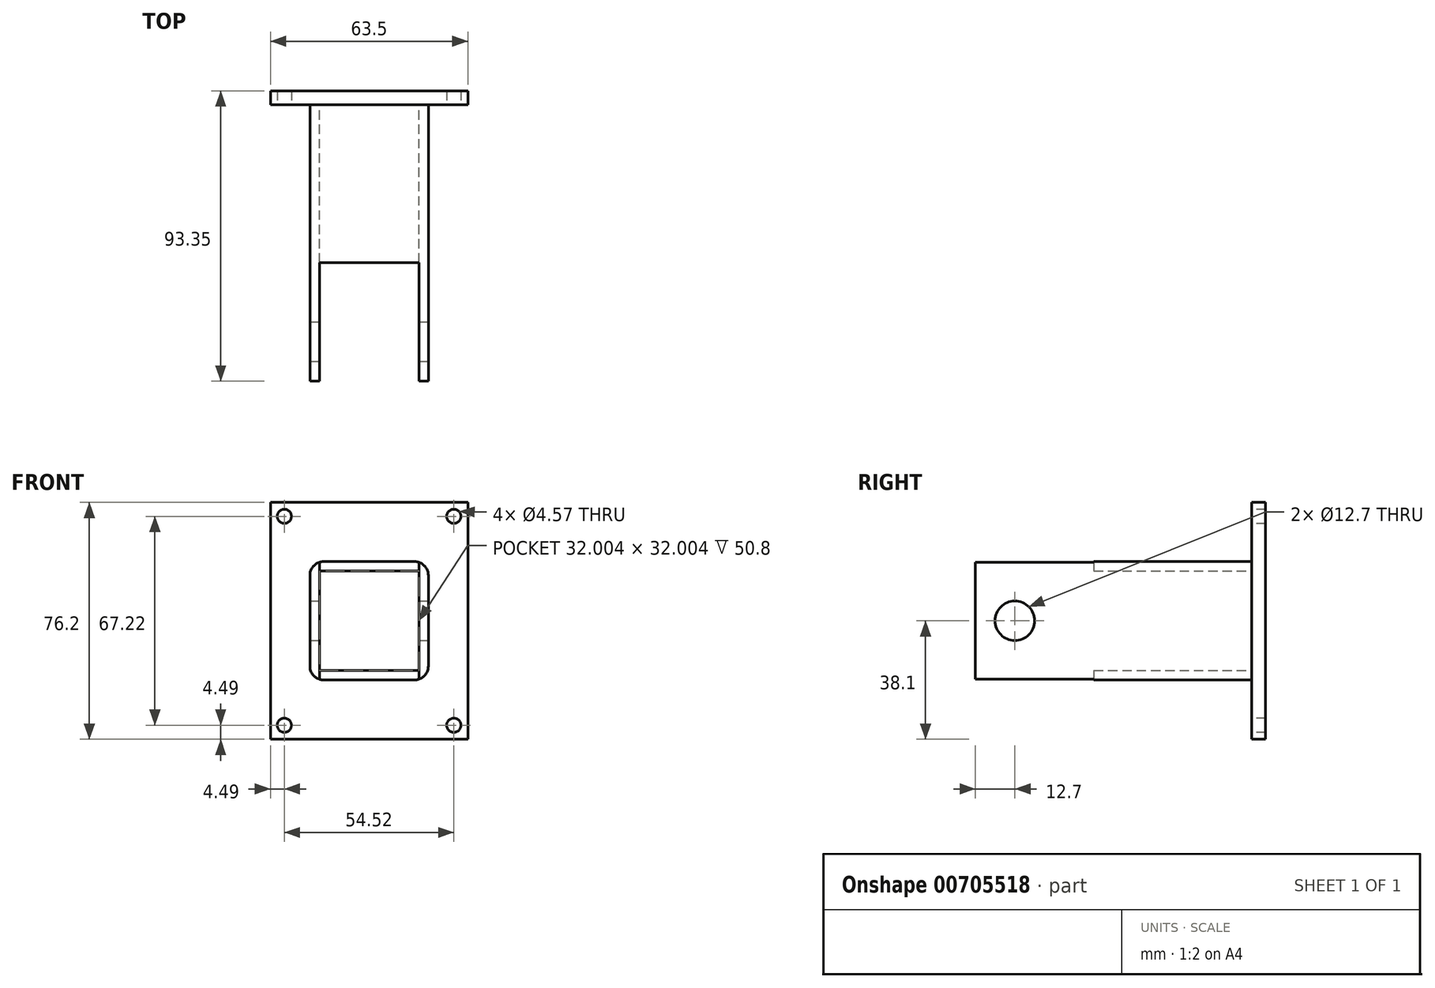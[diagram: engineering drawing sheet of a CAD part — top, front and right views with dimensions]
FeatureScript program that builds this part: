
annotation { "Feature Type Name" : "Feature", "Feature Type Description" : "" }
export const myFeature = defineFeature(function(context is Context, id is Id, definition is map)
    precondition{}
    {
        {
            var Q0;
            Q0=qCreatedBy(makeId("Front.planeOp"),FACE);
            var sketch = newSketch(context, id + "F0", { "sketchPlane" : qUnion([Q0])});
            skLineSegment(sketch, "E0.bottom", {"start": v(14.6, 19.05) * mm, "end": v(-14.6, 19.05) * mm});
            skLineSegment(sketch, "E0.top", {"start": v(14.6, -19.05) * mm, "end": v(-14.6, -19.05) * mm});
            skLineSegment(sketch, "E0.left", {"start": v(19.05, 14.6) * mm, "end": v(19.05, -14.6) * mm});
            skLineSegment(sketch, "E0.right", {"start": v(-19.05, 14.6) * mm, "end": v(-19.05, -14.6) * mm});
            skPoint(sketch, "E0.middle", {"position": v(0, 0) * mm});
            skPoint(sketch, "E1.visualSharp", {"position": v(-19.05, 19.05) * mm});
            skArc(sketch, "E1.filletArc", {"start": v(-14.6, 19.05) * mm, "mid": v(-17.75, 17.75) * mm, "end": v(-19.05, 14.6) * mm});
            skPoint(sketch, "E2.visualSharp", {"position": v(19.05, 19.05) * mm});
            skArc(sketch, "E2.filletArc", {"start": v(19.05, 14.6) * mm, "mid": v(17.75, 17.75) * mm, "end": v(14.6, 19.05) * mm});
            skPoint(sketch, "E3.visualSharp", {"position": v(19.05, -19.05) * mm});
            skArc(sketch, "E3.filletArc", {"start": v(14.6, -19.05) * mm, "mid": v(17.75, -17.75) * mm, "end": v(19.05, -14.6) * mm});
            skPoint(sketch, "E4.visualSharp", {"position": v(-19.05, -19.05) * mm});
            skArc(sketch, "E4.filletArc", {"start": v(-19.05, -14.6) * mm, "mid": v(-17.75, -17.75) * mm, "end": v(-14.6, -19.05) * mm});
            skLineSegment(sketch, "E5.0", {"start": v(16, 16) * mm, "end": v(-16, 16) * mm});
            skLineSegment(sketch, "E5.1", {"start": v(16, 16) * mm, "end": v(16, -16) * mm});
            skLineSegment(sketch, "E5.2", {"start": v(16, -16) * mm, "end": v(-16, -16) * mm});
            skLineSegment(sketch, "E5.3", {"start": v(-16, 16) * mm, "end": v(-16, -16) * mm});
            skSolve(sketch);
        }
        {
            var Q0;
            Q0=makeQuery(id+"F0.imprint","IMPRINT",FACE,{"disambiguationData":[TD([[makeQuery(id+"F0.imprint","IMPRINT",EDGE,{"derivedFrom":sQuery(id+"F0.wireOp",EDGE,"E0.bottom")}),1.0]])]});
            extrude(context, id + "F1", {"entities" : qUnion([Q0]), "depth" : 88.9 * mm, "offsetDistance" : 25.4 * mm});
        }
        {
            var Q0;
            Q0=qCreatedBy(makeId("Right.planeOp"),FACE);
            var sketch = newSketch(context, id + "F2", { "sketchPlane" : qUnion([Q0])});
            skLineSegment(sketch, "E6", {"start": v(-88.9, 0) * mm, "end": v(-76.2, 0) * mm, "construction": true});
            skCircle(sketch, "E7", {"center": v(-76.2, 0) * mm, "radius": 6.35 * mm});
            skSolve(sketch);
        }
        {
            var Q0;
            Q0 = qSketchRegion(id + "F2", true);
            extrude(context, id + "F3", {"entities" : qUnion([Q0]), "operationType" : NewBodyOperationType.REMOVE, "endBound" : BoundingType.SYMMETRIC, "oppositeDirection" : true, "depth" : 48.77 * mm, "offsetDistance" : 25.4 * mm});
        }
        {
            var Q0;
            Q0=makeQuery(id+"F1.opExtrude","CAP_FACE",FACE,{"disambiguationData":[OSD([sQuery(id+"F0.wireOp",EDGE,"E0.bottom"),sQuery(id+"F0.wireOp",EDGE,"E0.top"),sQuery(id+"F0.wireOp",EDGE,"E0.left"),sQuery(id+"F0.wireOp",EDGE,"E0.right"),sQuery(id+"F0.wireOp",EDGE,"E1.filletArc"),sQuery(id+"F0.wireOp",EDGE,"E2.filletArc"),sQuery(id+"F0.wireOp",EDGE,"E3.filletArc"),sQuery(id+"F0.wireOp",EDGE,"E4.filletArc"),sQuery(id+"F0.wireOp",EDGE,"E5.0"),sQuery(id+"F0.wireOp",EDGE,"E5.1"),sQuery(id+"F0.wireOp",EDGE,"E5.2"),sQuery(id+"F0.wireOp",EDGE,"E5.3")])],"isStart":false});
            cPlane(context, id + "F4", {"entities" : qUnion([Q0]), "cplaneType" : CPlaneType.OFFSET, "offset" : 0 * mm, "width" : 152.4 * mm, "height" : 152.4 * mm});
        }
        {
            var Q0;
            Q0=qCreatedBy(id+"F4.planeOp",FACE);
            var sketch = newSketch(context, id + "F5", { "sketchPlane" : qUnion([Q0])});
            skLineSegment(sketch, "E8.bottom", {"start": v(16, 25.4) * mm, "end": v(-16, 25.4) * mm});
            skLineSegment(sketch, "E8.top", {"start": v(16, -25.4) * mm, "end": v(-16, -25.4) * mm});
            skLineSegment(sketch, "E8.left", {"start": v(16, 25.4) * mm, "end": v(16, -25.4) * mm});
            skLineSegment(sketch, "E8.right", {"start": v(-16, 25.4) * mm, "end": v(-16, -25.4) * mm});
            skPoint(sketch, "E8.middle", {"position": v(0, 0) * mm});
            skSolve(sketch);
        }
        {
            var Q0;
            Q0 = qSketchRegion(id + "F5", true);
            extrude(context, id + "F6", {"entities" : qUnion([Q0]), "operationType" : NewBodyOperationType.REMOVE, "oppositeDirection" : true, "depth" : 38.1 * mm, "offsetDistance" : 25.4 * mm});
        }
        {
            var Q0;
            Q0=qCreatedBy(makeId("Front.planeOp"),FACE);
            var sketch = newSketch(context, id + "F7", { "sketchPlane" : qUnion([Q0])});
            skLineSegment(sketch, "E9.bottom", {"start": v(-31.75, 38.1) * mm, "end": v(31.75, 38.1) * mm});
            skLineSegment(sketch, "E9.top", {"start": v(-31.75, -38.1) * mm, "end": v(31.75, -38.1) * mm});
            skLineSegment(sketch, "E9.left", {"start": v(-31.75, 38.1) * mm, "end": v(-31.75, -38.1) * mm});
            skLineSegment(sketch, "E9.right", {"start": v(31.75, 38.1) * mm, "end": v(31.75, -38.1) * mm});
            skPoint(sketch, "E9.middle", {"position": v(0, 0) * mm});
            skSolve(sketch);
        }
        {
            var Q0;
            Q0 = qSketchRegion(id + "F7", true);
            extrude(context, id + "F8", {"entities" : qUnion([Q0]), "operationType" : NewBodyOperationType.ADD, "oppositeDirection" : true, "depth" : 4.44 * mm, "offsetDistance" : 25.4 * mm});
        }
        {
            var Q0;
            {var subQ0=sQuery(id+"F7.wireOp",EDGE,"E9.bottom");var subQ1=sQuery(id+"F7.wireOp",EDGE,"E9.right");var subQ2=sQuery(id+"F7.wireOp",EDGE,"E9.left");var subQ3=sQuery(id+"F7.wireOp",EDGE,"E9.top");Q0=makeQuery(id+"F8.boolean.opBoolean","SPLIT",FACE,{"disambiguationData":[TD([makeQuery(id+"F1.opExtrude","SWEPT_FACE",FACE,{"disambiguationData":[OSD([sQuery(id+"F0.wireOp",EDGE,"E0.bottom")])]})])],"derivedFrom":makeQuery(id+"F8.opExtrude","CAP_FACE",FACE,{"disambiguationData":[OSD([subQ0,subQ3,subQ2,subQ1])],"isStart":true})});}
            var sketch = newSketch(context, id + "F9", { "sketchPlane" : qUnion([Q0])});
            skCircle(sketch, "E10", {"center": v(-27.26, 33.6) * mm, "radius": 2.29 * mm});
            skCircle(sketch, "E11", {"center": v(27.26, 33.6) * mm, "radius": 2.29 * mm});
            skCircle(sketch, "E12", {"center": v(27.26, -33.6) * mm, "radius": 2.29 * mm});
            skCircle(sketch, "E13", {"center": v(-27.26, -33.6) * mm, "radius": 2.29 * mm});
            skLineSegment(sketch, "E14", {"start": v(-31.75, 38.1) * mm, "end": v(-27.26, 33.6) * mm, "construction": true});
            skLineSegment(sketch, "E15", {"start": v(31.75, 38.1) * mm, "end": v(27.26, 33.6) * mm, "construction": true});
            skLineSegment(sketch, "E16", {"start": v(-31.75, -38.1) * mm, "end": v(-27.26, -33.6) * mm, "construction": true});
            skLineSegment(sketch, "E17", {"start": v(31.75, -38.1) * mm, "end": v(27.26, -33.6) * mm});
            skSolve(sketch);
        }
        {
            var Q0;
            Q0=makeQuery(id+"F9.imprint","IMPRINT",FACE,{"disambiguationData":[TD([[makeQuery(id+"F9.imprint","IMPRINT",EDGE,{"derivedFrom":sQuery(id+"F9.wireOp",EDGE,"E11")}),1.0]])]});
            var Q1;
            Q1=makeQuery(id+"F9.imprint","IMPRINT",FACE,{"disambiguationData":[TD([[makeQuery(id+"F9.imprint","IMPRINT",EDGE,{"derivedFrom":sQuery(id+"F9.wireOp",EDGE,"E12")}),1.0]])]});
            var Q2;
            Q2=makeQuery(id+"F9.imprint","IMPRINT",FACE,{"disambiguationData":[TD([[makeQuery(id+"F9.imprint","IMPRINT",EDGE,{"derivedFrom":sQuery(id+"F9.wireOp",EDGE,"E13")}),1.0]])]});
            var Q3;
            Q3=makeQuery(id+"F9.imprint","IMPRINT",FACE,{"disambiguationData":[TD([[makeQuery(id+"F9.imprint","IMPRINT",EDGE,{"derivedFrom":sQuery(id+"F9.wireOp",EDGE,"E10")}),1.0]])]});
            extrude(context, id + "F10", {"entities" : qUnion([Q0, Q1, Q2, Q3]), "operationType" : NewBodyOperationType.REMOVE, "oppositeDirection" : true, "depth" : 25.4 * mm, "offsetDistance" : 25.4 * mm});
        }
    });
